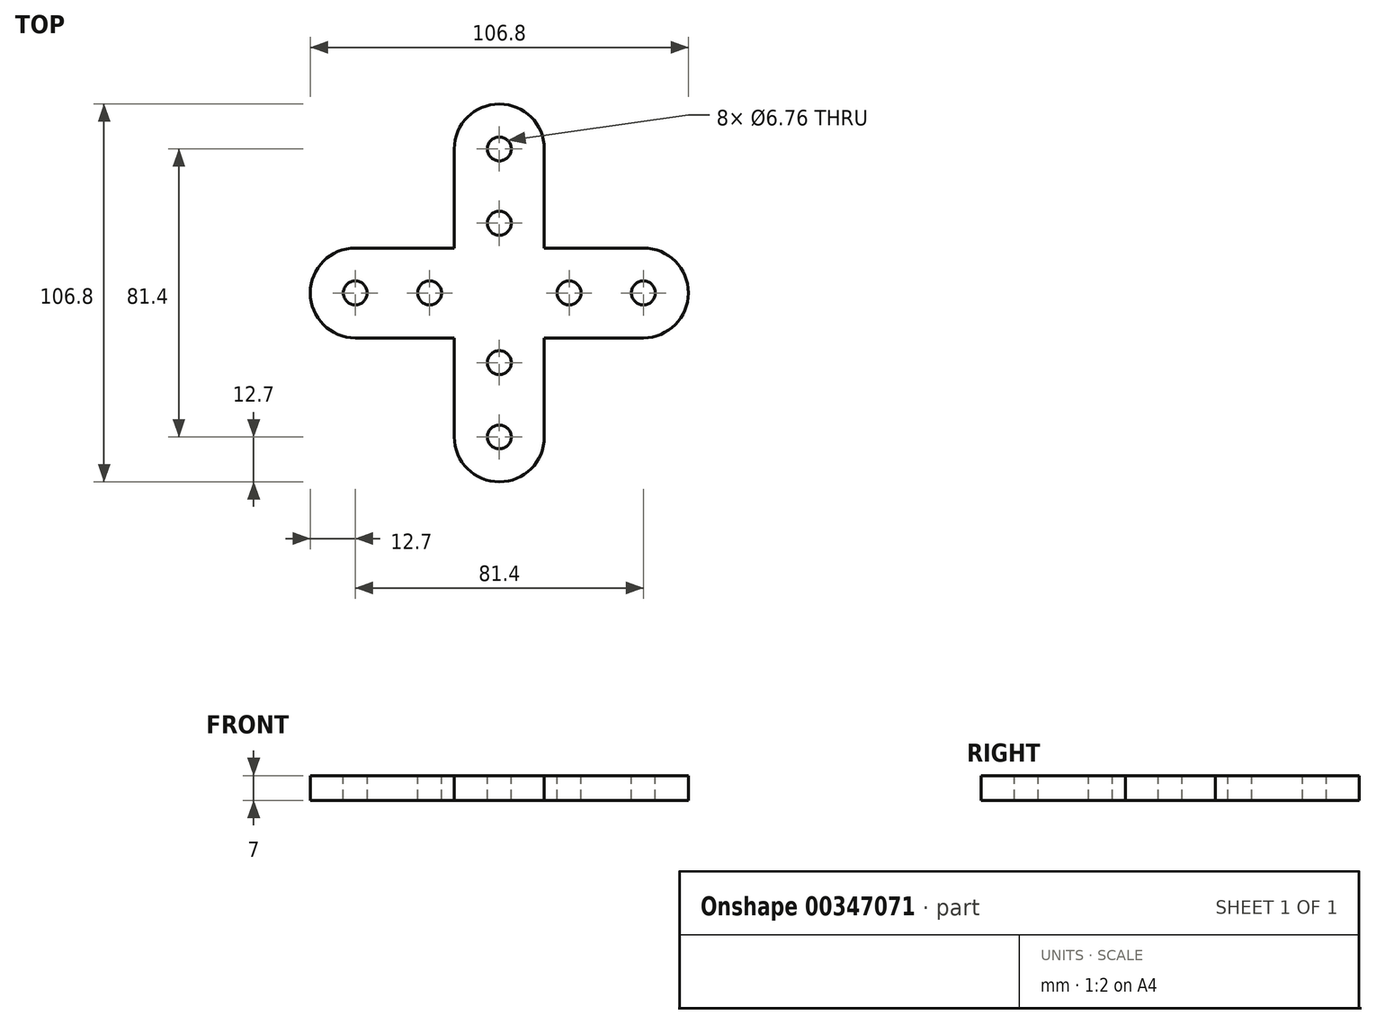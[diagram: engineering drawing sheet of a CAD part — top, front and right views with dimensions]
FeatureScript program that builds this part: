
annotation { "Feature Type Name" : "Feature", "Feature Type Description" : "" }
export const myFeature = defineFeature(function(context is Context, id is Id, definition is map)
    precondition{}
    {
        {
            var Q0;
            Q0=qCreatedBy(makeId("Top.planeOp"),FACE);
            var sketch = newSketch(context, id + "F0", { "sketchPlane" : qUnion([Q0])});
            skLineSegment(sketch, "E0.bottom", {"start": v(-12.7, 63.5) * mm, "end": v(12.7, 63.5) * mm, "construction": true});
            skLineSegment(sketch, "E0.top", {"start": v(-12.7, -63.5) * mm, "end": v(12.7, -63.5) * mm, "construction": true});
            skLineSegment(sketch, "E0.left", {"start": v(-12.7, 63.5) * mm, "end": v(-12.7, -63.5) * mm, "construction": true});
            skLineSegment(sketch, "E0.right", {"start": v(12.7, 63.5) * mm, "end": v(12.7, -63.5) * mm, "construction": true});
            skPoint(sketch, "E0.middle", {"position": v(0, 0) * mm});
            skLineSegment(sketch, "E1.bottom", {"start": v(63.5, -12.7) * mm, "end": v(12.7, -12.7) * mm, "construction": true});
            skLineSegment(sketch, "E1.top", {"start": v(63.5, 12.7) * mm, "end": v(12.7, 12.7) * mm, "construction": true});
            skLineSegment(sketch, "E1.left", {"start": v(63.5, -12.7) * mm, "end": v(63.5, 12.7) * mm, "construction": true});
            skLineSegment(sketch, "E1.right", {"start": v(-63.5, -12.7) * mm, "end": v(-63.5, 12.7) * mm, "construction": true});
            skLineSegment(sketch, "E2.trimOffspring", {"start": v(-12.7, 12.7) * mm, "end": v(-63.5, 12.7) * mm, "construction": true});
            skLineSegment(sketch, "E3.trimOffspring", {"start": v(-12.7, -12.7) * mm, "end": v(-63.5, -12.7) * mm, "construction": true});
            skSolve(sketch);
        }
        {
            var Q0;
            Q0=qCreatedBy(makeId("Top.planeOp"),FACE);
            var sketch = newSketch(context, id + "F1", { "sketchPlane" : qUnion([Q0])});
            skPoint(sketch, "E4", {"position": v(-12.7, 0) * mm});
            skPoint(sketch, "E5", {"position": v(-19.7, 0) * mm});
            skLineSegment(sketch, "E6", {"start": v(-12.7, 0) * mm, "end": v(-40.7, 0) * mm, "construction": true});
            skLineSegment(sketch, "E7.0", {"start": v(-12.7, 12.7) * mm, "end": v(-63.5, 12.7) * mm, "construction": true});
            skLineSegment(sketch, "E8.0", {"start": v(-12.7, -12.7) * mm, "end": v(-63.5, -12.7) * mm, "construction": true});
            skLineSegment(sketch, "E9.0", {"start": v(-12.7, 63.5) * mm, "end": v(-12.7, -63.5) * mm, "construction": true});
            skLineSegment(sketch, "E10", {"start": v(-40.7, 12.7) * mm, "end": v(-28.5, 12.7) * mm});
            skLineSegment(sketch, "E11", {"start": v(-40.7, -12.7) * mm, "end": v(-28.5, -12.7) * mm});
            skArc(sketch, "E12", {"start": v(-40.7, 12.7) * mm, "mid": v(-53.4, 0) * mm, "end": v(-40.7, -12.7) * mm});
            skLineSegment(sketch, "E13", {"start": v(-40.7, 12.7) * mm, "end": v(-12.7, 12.7) * mm});
            skLineSegment(sketch, "E14", {"start": v(0, 0) * mm, "end": v(-12.7, -12.7) * mm});
            skLineSegment(sketch, "E15", {"start": v(0, 0) * mm, "end": v(-12.7, 12.7) * mm});
            skLineSegment(sketch, "E16", {"start": v(-12.7, -12.7) * mm, "end": v(-28.5, -12.7) * mm});
            skSolve(sketch);
        }
        {
            var Q0;
            Q0=qCreatedBy(makeId("Front.planeOp"),FACE);
            var sketch = newSketch(context, id + "F2", { "sketchPlane" : qUnion([Q0])});
            skLineSegment(sketch, "E17", {"start": v(0, 0) * mm, "end": v(0, 30.66) * mm, "construction": true});
            skSolve(sketch);
        }
        {
            var Q0;
            Q0=makeQuery(id+"F1.imprint","IMPRINT",FACE,{"disambiguationData":[TD([[makeQuery(id+"F1.imprint","IMPRINT",EDGE,{"derivedFrom":sQuery(id+"F1.wireOp",EDGE,"E11")}),1.0]])]});
            extrude(context, id + "F3", {"entities" : qUnion([Q0]), "depth" : 7 * mm});
        }
        {
            var Q0;
            Q0=sQuery(id+"F1.wireOp",VERTEX,"E6.end");
            var Q1;
            Q1=sQuery(id+"F1.wireOp",VERTEX,"E5");
            var Q2;
            Q2=makeQuery(id+"F3.opExtrude","SWEPT_BODY",BODY,{"disambiguationData":[OSD([sQuery(id+"F1.wireOp",EDGE,"E11"),sQuery(id+"F1.wireOp",EDGE,"E12"),sQuery(id+"F1.wireOp",EDGE,"E13"),sQuery(id+"F1.wireOp",EDGE,"E14"),sQuery(id+"F1.wireOp",EDGE,"E15"),sQuery(id+"F1.wireOp",EDGE,"E16")])]});
            hole(context, id + "F4", {"style" : HoleStyle.SIMPLE, "endStyle" : HoleEndStyle.THROUGH, "oppositeDirection" : true, "standardTappedOrClearance" : lookupTablePath({ "standard" : "ANSI", "fit" : "Normal (ASME)", "size" : "1/4", "type" : "Clearance" }), "standardBlindInLast" : lookupTablePath({ "fit" : "Free", "standard" : "ANSI", "size" : "1/4", "type" : "Clearance" }), "holeDiameter" : 6.76 * mm, "isTappedThrough" : true, "tappedDepth" : 12 * mm, "tapClearance" : 3, "locations" : qUnion([Q0, Q1]), "scope" : qUnion([Q2]), "startStyle" : HoleStartStyle.PART});
        }
        {
            var Q0;
            Q0=makeQuery(id+"F3.opExtrude","SWEPT_BODY",BODY,{"disambiguationData":[OSD([sQuery(id+"F1.wireOp",EDGE,"E11"),sQuery(id+"F1.wireOp",EDGE,"E12"),sQuery(id+"F1.wireOp",EDGE,"E13"),sQuery(id+"F1.wireOp",EDGE,"E14"),sQuery(id+"F1.wireOp",EDGE,"E15"),sQuery(id+"F1.wireOp",EDGE,"E16")])]});
            var Q1;
            Q1=sQuery(id+"F2.wireOp",EDGE,"E17");
            circularPattern(context, id + "F5", {"operationType" : NewBodyOperationType.ADD, "entities" : qUnion([Q0]), "axis" : qUnion([Q1]), "angle" : 360 * degree, "instanceCount" : 4, "equalSpace" : true, "computeTransformsWithoutBuiltin" : true});
        }
    });
